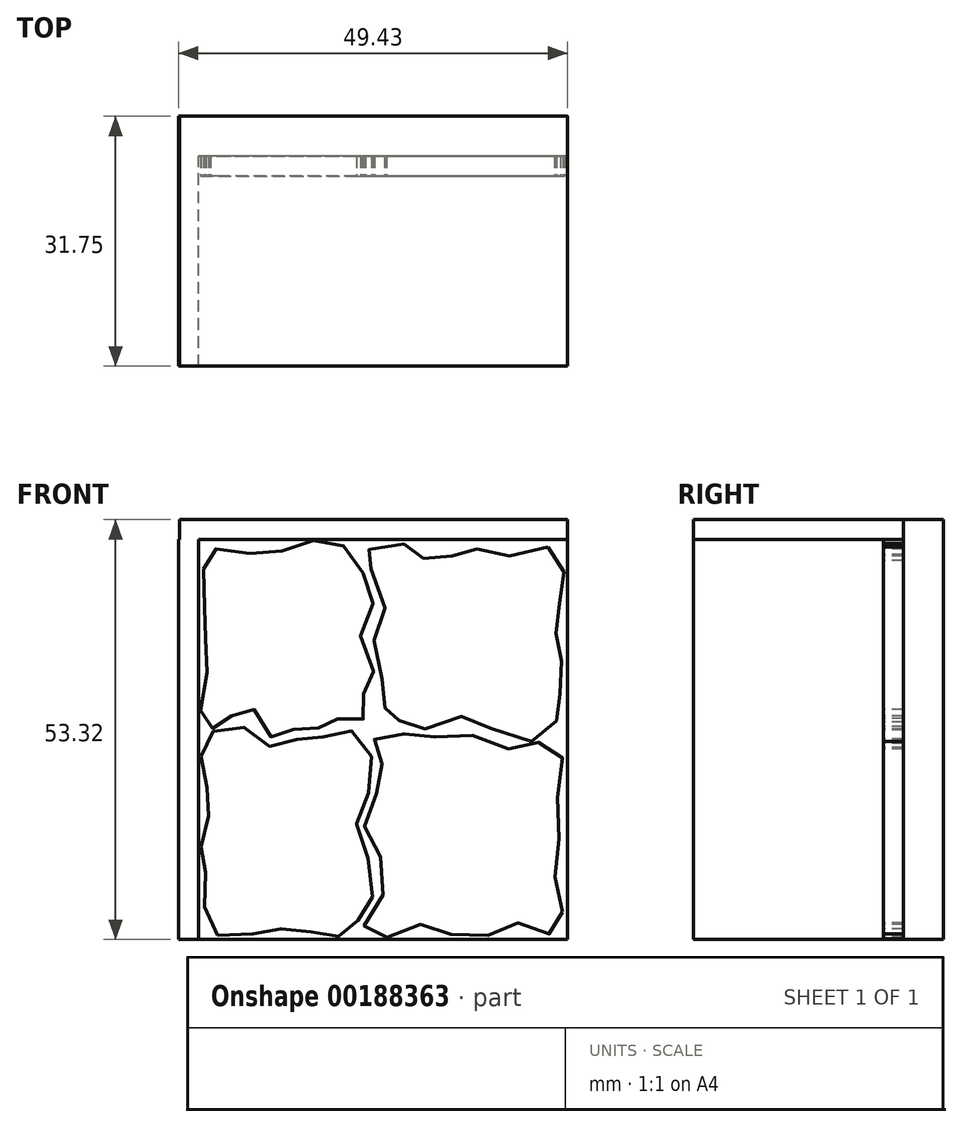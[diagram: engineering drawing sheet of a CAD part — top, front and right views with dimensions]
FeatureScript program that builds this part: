
annotation { "Feature Type Name" : "Feature", "Feature Type Description" : "" }
export const myFeature = defineFeature(function(context is Context, id is Id, definition is map)
    precondition{}
    {
        {
            var Q0;
            Q0=qCreatedBy(makeId("Front.planeOp"),FACE);
            var sketch = newSketch(context, id + "F0", { "sketchPlane" : qUnion([Q0])});
            skLineSegment(sketch, "E0.bottom", {"start": v(-24.63, -26.66) * mm, "end": v(24.63, -26.66) * mm});
            skLineSegment(sketch, "E0.top", {"start": v(-24.63, 26.66) * mm, "end": v(24.63, 26.66) * mm});
            skLineSegment(sketch, "E0.left", {"start": v(-24.63, -26.66) * mm, "end": v(-24.63, 26.66) * mm});
            skLineSegment(sketch, "E0.right", {"start": v(24.63, -26.66) * mm, "end": v(24.63, 26.66) * mm});
            skPoint(sketch, "E0.middle", {"position": v(0, 0) * mm});
            skSolve(sketch);
        }
        {
            var Q0;
            Q0=makeQuery(id+"F0.imprint","IMPRINT",FACE,{"disambiguationData":[TD([[makeQuery(id+"F0.imprint","IMPRINT",EDGE,{"derivedFrom":sQuery(id+"F0.wireOp",EDGE,"E0.bottom")}),1.0]])]});
            extrude(context, id + "F1", {"entities" : qUnion([Q0]), "depth" : 5.08 * mm});
        }
        {
            var Q0;
            Q0=qCreatedBy(makeId("Front.planeOp"),FACE);
            var sketch = newSketch(context, id + "F2", { "sketchPlane" : qUnion([Q0])});
            skLineSegment(sketch, "E1.bottom", {"start": v(-24.66, 26.65) * mm, "end": v(24.6, 26.65) * mm});
            skLineSegment(sketch, "E1.top", {"start": v(-24.66, 24.13) * mm, "end": v(24.6, 24.13) * mm});
            skLineSegment(sketch, "E1.left", {"start": v(-24.66, 26.65) * mm, "end": v(-24.66, 24.13) * mm});
            skLineSegment(sketch, "E1.right", {"start": v(24.6, 26.65) * mm, "end": v(24.6, 24.13) * mm});
            skLineSegment(sketch, "E2.bottom", {"start": v(-24.8, -26.66) * mm, "end": v(-22.28, -26.66) * mm});
            skLineSegment(sketch, "E2.top", {"start": v(-24.8, 24.13) * mm, "end": v(-22.28, 24.13) * mm});
            skLineSegment(sketch, "E2.left", {"start": v(-24.8, -26.66) * mm, "end": v(-24.8, 24.13) * mm});
            skLineSegment(sketch, "E2.right", {"start": v(-22.28, -26.66) * mm, "end": v(-22.28, 24.13) * mm});
            skSolve(sketch);
        }
        {
            var Q0;
            Q0 = qSketchRegion(id + "F2", true);
            extrude(context, id + "F3", {"entities" : qUnion([Q0]), "operationType" : NewBodyOperationType.ADD, "depth" : 31.75 * mm});
        }
        {
            var Q0;
            Q0=qCreatedBy(makeId("Front.planeOp"),FACE);
            var sketch = newSketch(context, id + "F4", { "sketchPlane" : qUnion([Q0])});
            skFitSpline(sketch, "E3", {"points": [v(-19.82, -26.17) * mm, v(-21.5, -22.8) * mm, v(-21.36, -18.2) * mm, v(-21.92, -15.67) * mm, v(-21.36, -12.31) * mm, v(-20.8, -8.68) * mm, v(-21.78, -5.88) * mm, v(-21.5, -1.54) * mm, v(-19.82, 0) * mm, v(-15.76, 0) * mm, v(-12.96, -2.24) * mm, v(-9.75, -1.26) * mm, v(-7.37, -1.26) * mm, v(-3.87, 0) * mm, v(-1.35, -1.54) * mm, v(0, -6.16) * mm, v(-2.05, -10.91) * mm, v(-1.5, -14.41) * mm, v(0, -20.7) * mm, v(-1.63, -23.23) * mm, v(-2.75, -25.75) * mm, v(-5.97, -26.17) * mm, v(-8.49, -25.6) * mm, v(-12.13, -25.33) * mm, v(-15.06, -25.89) * mm, v(-19.82, -26.17) * mm]});
            skSolve(sketch);
        }
        {
            var Q0;
            Q0 = qSketchRegion(id + "F4", true);
            extrude(context, id + "F5", {"entities" : qUnion([Q0]), "operationType" : NewBodyOperationType.ADD, "depth" : 7.62 * mm});
        }
        {
            var Q0;
            Q0=qCreatedBy(makeId("Front.planeOp"),FACE);
            var sketch = newSketch(context, id + "F6", { "sketchPlane" : qUnion([Q0])});
            skFitSpline(sketch, "E4", {"points": [v(-22, 2.44) * mm, v(-20.73, 0) * mm, v(-19.33, 1.46) * mm, v(-16.95, 1.88) * mm, v(-15, 2.44) * mm, v(-12.76, -1.2) * mm, v(-10.24, 0) * mm, v(-7.44, 0) * mm, v(-5.76, 1.32) * mm, v(-3.38, 1.04) * mm, v(-1.14, 1.6) * mm, v(-1.28, 4.54) * mm, v(0, 6.78) * mm, v(-1.7, 11.96) * mm, v(0, 16.58) * mm, v(-2.12, 20.91) * mm, v(-4.64, 23.85) * mm, v(-9.26, 23.57) * mm, v(-13.18, 22.31) * mm, v(-18.07, 22.73) * mm, v(-21.3, 22.45) * mm, v(-21.43, 17.42) * mm, v(-21.57, 12.8) * mm, v(-21.01, 8.46) * mm, v(-22, 2.44) * mm]});
            skSolve(sketch);
        }
        {
            var Q0;
            Q0 = qSketchRegion(id + "F6", true);
            extrude(context, id + "F7", {"entities" : qUnion([Q0]), "operationType" : NewBodyOperationType.ADD, "depth" : 7.62 * mm});
        }
        {
            var Q0;
            Q0=qCreatedBy(makeId("Front.planeOp"),FACE);
            var sketch = newSketch(context, id + "F8", { "sketchPlane" : qUnion([Q0])});
            skFitSpline(sketch, "E5", {"points": [v(23.97, -23.17) * mm, v(23.13, -25.82) * mm, v(20.9, -25.54) * mm, v(17.82, -24.56) * mm, v(15.02, -25.96) * mm, v(10.68, -26.38) * mm, v(7.88, -24.98) * mm, v(4.52, -25.12) * mm, v(1.02, -26.52) * mm, v(-1.21, -25.54) * mm, v(0, -22.89) * mm, v(1.58, -19.25) * mm, v(0, -14.63) * mm, v(-1.21, -12.11) * mm, v(0, -8.61) * mm, v(1.58, -5.53) * mm, v(0, -3.01) * mm, v(0, -1.34) * mm, v(3.26, 0) * mm, v(4.94, -1.76) * mm, v(10.4, 0) * mm, v(13.62, -1.48) * mm, v(17.82, -2.46) * mm, v(20.48, -1.76) * mm, v(22.71, -1.76) * mm, v(24.25, -5.67) * mm, v(23, -10.15) * mm, v(23.7, -15.47) * mm, v(23, -19.39) * mm, v(23.97, -23.17) * mm]});
            skSolve(sketch);
        }
        {
            var Q0;
            Q0 = qSketchRegion(id + "F8", true);
            extrude(context, id + "F9", {"entities" : qUnion([Q0]), "operationType" : NewBodyOperationType.ADD, "depth" : 7.62 * mm});
        }
        {
            var Q0;
            Q0=qCreatedBy(makeId("Front.planeOp"),FACE);
            var sketch = newSketch(context, id + "F10", { "sketchPlane" : qUnion([Q0])});
            skFitSpline(sketch, "E6", {"points": [v(22.15, 23.15) * mm, v(23.83, 21.2) * mm, v(24.11, 17.14) * mm, v(23, 14.76) * mm, v(23.41, 11.12) * mm, v(23.83, 8.88) * mm, v(23.83, 5.1) * mm, v(23, 2.72) * mm, v(23, 0) * mm, v(17.96, -1.48) * mm, v(13.2, 1.32) * mm, v(10.26, 1.46) * mm, v(5.64, 0) * mm, v(3.4, 1.04) * mm, v(1.58, 1.6) * mm, v(1.44, 3.14) * mm, v(1.16, 5.94) * mm, v(0, 10.98) * mm, v(1.3, 14.48) * mm, v(0, 19.93) * mm, v(-1.5, 22.17) * mm, v(1.44, 23.43) * mm, v(4.66, 23.3) * mm, v(6.06, 21.9) * mm, v(8.86, 21.61) * mm, v(10.96, 22.6) * mm, v(13.34, 22.87) * mm, v(16.98, 22.03) * mm, v(22.15, 23.15) * mm]});
            skSolve(sketch);
        }
        {
            var Q0;
            Q0 = qSketchRegion(id + "F10", true);
            extrude(context, id + "F11", {"entities" : qUnion([Q0]), "operationType" : NewBodyOperationType.ADD, "depth" : 7.62 * mm});
        }
    });
